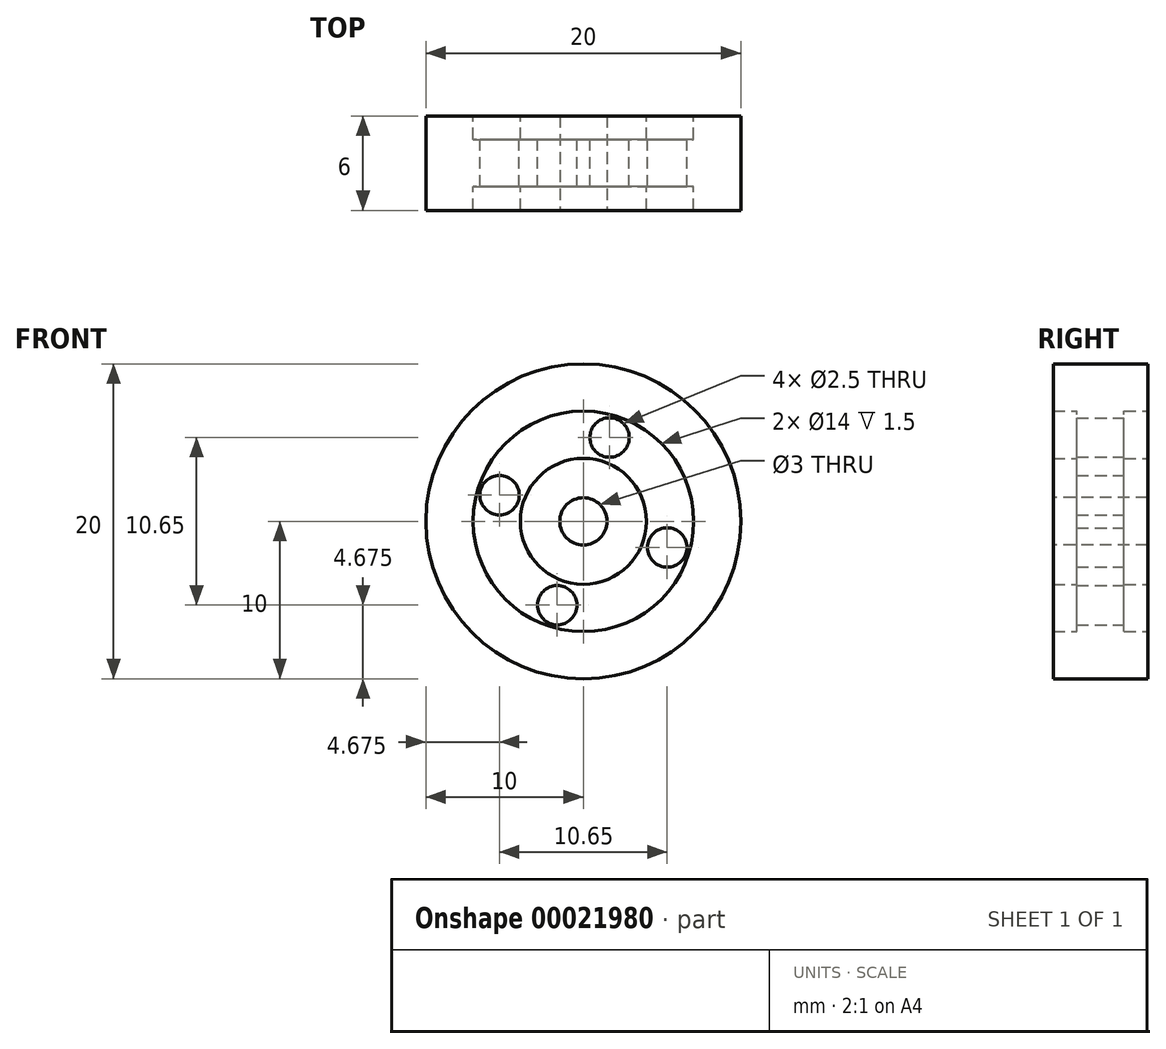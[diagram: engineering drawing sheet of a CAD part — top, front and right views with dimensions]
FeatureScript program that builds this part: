
annotation { "Feature Type Name" : "Feature", "Feature Type Description" : "" }
export const myFeature = defineFeature(function(context is Context, id is Id, definition is map)
    precondition{}
    {
        {
            var Q0;
            Q0=qCreatedBy(makeId("Front.planeOp"),FACE);
            var sketch = newSketch(context, id + "F0", { "sketchPlane" : qUnion([Q0])});
            skCircle(sketch, "E0", {"center": v(0, 0) * mm, "radius": 10 * mm});
            skCircle(sketch, "E1", {"center": v(0, 0) * mm, "radius": 7 * mm});
            skCircle(sketch, "E2", {"center": v(0, 0) * mm, "radius": 4 * mm});
            skCircle(sketch, "E3", {"center": v(1.66, 5.33) * mm, "radius": 1.25 * mm});
            skCircle(sketch, "E4.1.0", {"center": v(-5.33, 1.66) * mm, "radius": 1.25 * mm});
            skCircle(sketch, "E4.2.0", {"center": v(-1.66, -5.33) * mm, "radius": 1.25 * mm});
            skCircle(sketch, "E4.3.0", {"center": v(5.33, -1.66) * mm, "radius": 1.25 * mm});
            skSolve(sketch);
        }
        {
            var Q0;
            Q0=makeQuery(id+"F0.imprint","IMPRINT",FACE,{"disambiguationData":[TD([[makeQuery(id+"F0.imprint","IMPRINT",EDGE,{"derivedFrom":sQuery(id+"F0.wireOp",EDGE,"E1")}),1.0]])]});
            extrude(context, id + "F1", {"entities" : qUnion([Q0]), "endBound" : BoundingType.SYMMETRIC, "depth" : 3 * mm});
        }
        {
            var Q0;
            Q0=makeQuery(id+"F0.imprint","IMPRINT",FACE,{"disambiguationData":[TD([[makeQuery(id+"F0.imprint","IMPRINT",EDGE,{"derivedFrom":sQuery(id+"F0.wireOp",EDGE,"E2")}),1.0]])]});
            var Q1;
            Q1=makeQuery(id+"F0.imprint","IMPRINT",FACE,{"disambiguationData":[TD([[makeQuery(id+"F0.imprint","IMPRINT",EDGE,{"derivedFrom":sQuery(id+"F0.wireOp",EDGE,"E0")}),1.0]])]});
            extrude(context, id + "F2", {"entities" : qUnion([Q0, Q1]), "operationType" : NewBodyOperationType.ADD, "endBound" : BoundingType.SYMMETRIC, "depth" : 6 * mm});
        }
        {
            var Q0;
            Q0=makeQuery(id+"F2.opExtrude","CAP_FACE",FACE,{"disambiguationData":[OSD([sQuery(id+"F0.wireOp",EDGE,"E2")])],"isStart":false});
            var sketch = newSketch(context, id + "F3", { "sketchPlane" : qUnion([Q0])});
            skCircle(sketch, "E5", {"center": v(0, 0) * mm, "radius": 1.5 * mm});
            skSolve(sketch);
        }
        {
            var Q0;
            Q0=makeQuery(id+"F3.imprint","IMPRINT",FACE,{"disambiguationData":[TD([[makeQuery(id+"F3.imprint","IMPRINT",EDGE,{"derivedFrom":sQuery(id+"F3.wireOp",EDGE,"E5")}),1.0]])]});
            extrude(context, id + "F4", {"entities" : qUnion([Q0]), "operationType" : NewBodyOperationType.REMOVE, "oppositeDirection" : true, "depth" : 6 * mm});
        }
    });
